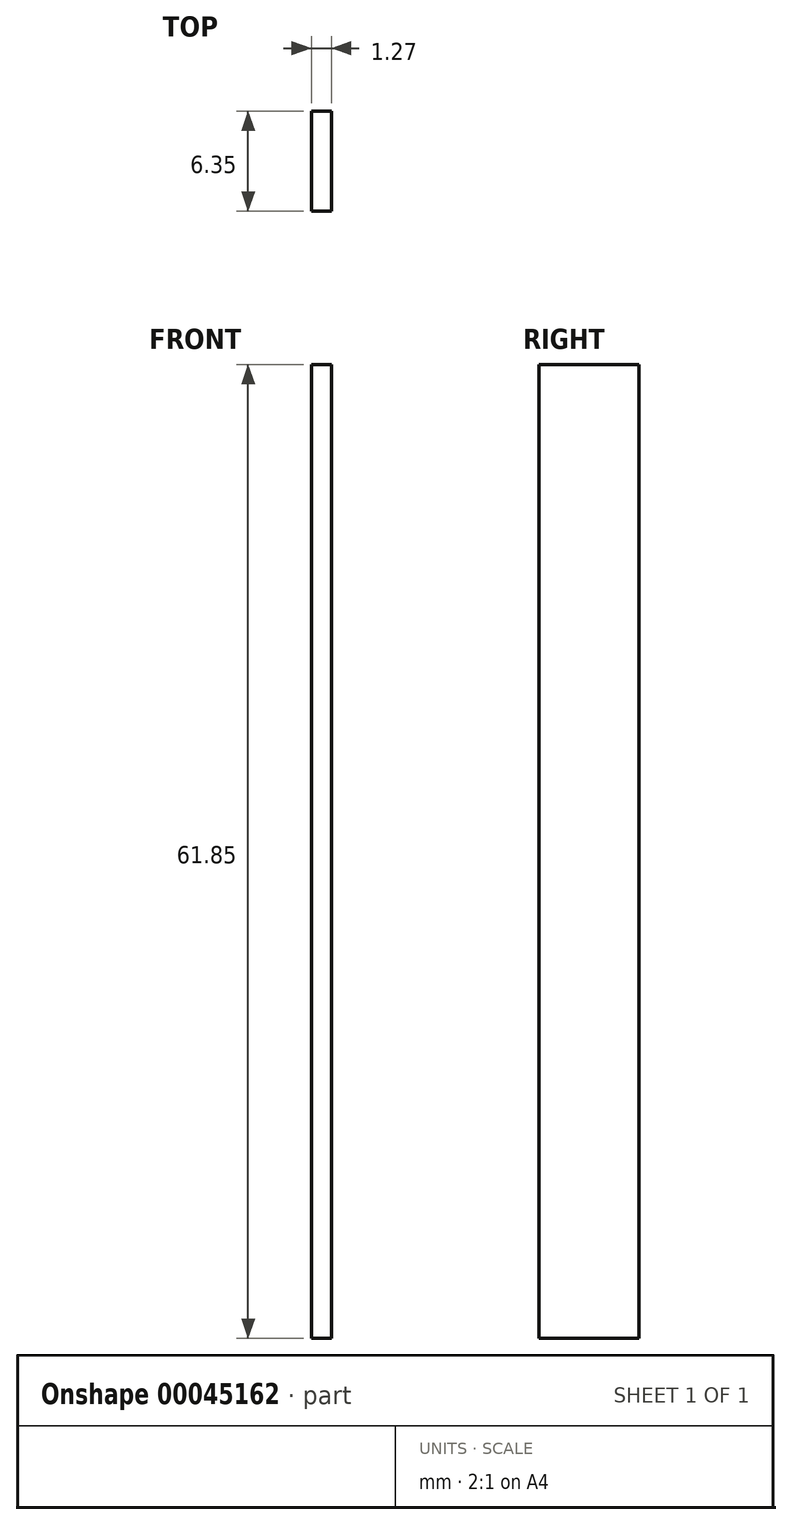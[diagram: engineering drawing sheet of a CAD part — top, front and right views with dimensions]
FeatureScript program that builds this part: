
annotation { "Feature Type Name" : "Feature", "Feature Type Description" : "" }
export const myFeature = defineFeature(function(context is Context, id is Id, definition is map)
    precondition{}
    {
        {
            var Q0;
            Q0=qCreatedBy(makeId("Front.planeOp"),FACE);
            var sketch = newSketch(context, id + "F0", { "sketchPlane" : qUnion([Q0])});
            skLineSegment(sketch, "E0", {"start": v(0, 0) * mm, "end": v(0, 61.85) * mm});
            skLineSegment(sketch, "E1", {"start": v(0, 61.85) * mm, "end": v(1.27, 61.85) * mm});
            skLineSegment(sketch, "E2", {"start": v(1.27, 61.85) * mm, "end": v(1.27, 0) * mm});
            skLineSegment(sketch, "E3", {"start": v(1.27, 0) * mm, "end": v(0, 0) * mm});
            skSolve(sketch);
        }
        {
            var Q0;
            Q0 = qSketchRegion(id + "F0", true);
            extrude(context, id + "F1", {"entities" : qUnion([Q0]), "depth" : 6.35 * mm});
        }
    });
